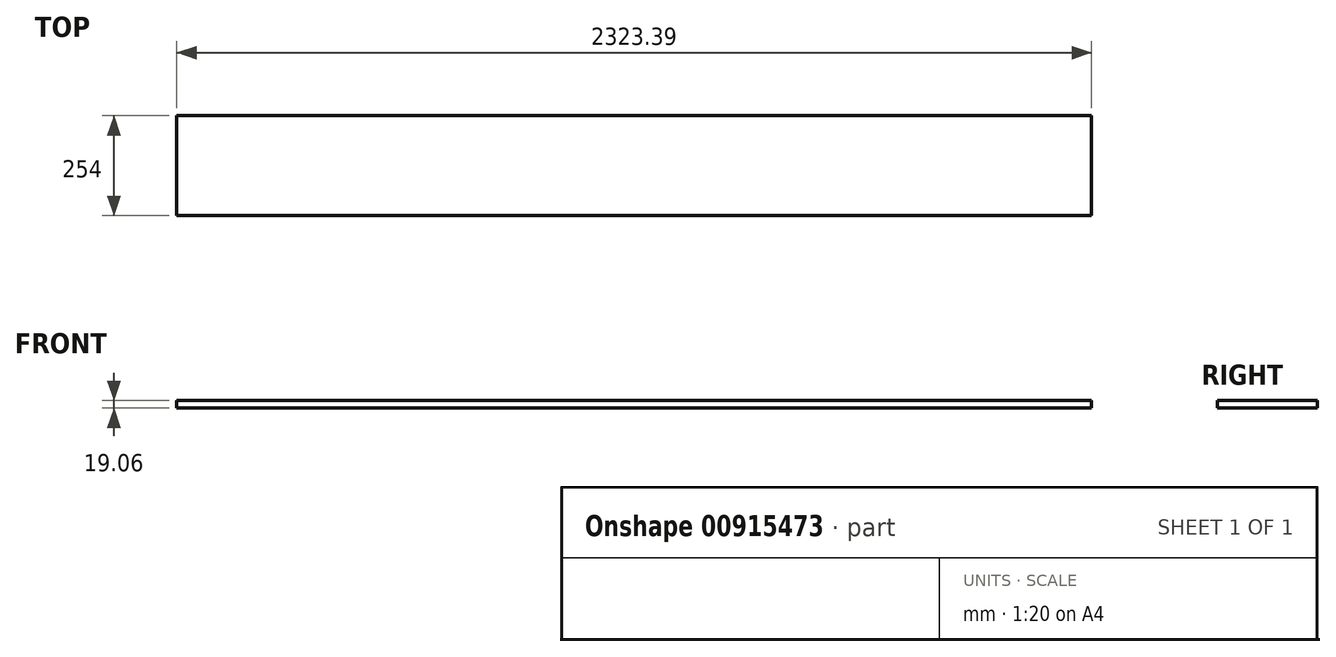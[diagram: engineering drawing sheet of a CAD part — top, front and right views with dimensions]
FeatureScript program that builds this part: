
annotation { "Feature Type Name" : "Feature", "Feature Type Description" : "" }
export const myFeature = defineFeature(function(context is Context, id is Id, definition is map)
    precondition{}
    {
        {
            var Q0;
            Q0=qCreatedBy(makeId("Right.planeOp"),FACE);
            var sketch = newSketch(context, id + "F0", { "sketchPlane" : qUnion([Q0])});
            skLineSegment(sketch, "E0.bottom", {"start": v(127, 9.53) * mm, "end": v(-127, 9.53) * mm});
            skLineSegment(sketch, "E0.top", {"start": v(127, -9.53) * mm, "end": v(-127, -9.53) * mm});
            skLineSegment(sketch, "E0.left", {"start": v(127, 9.53) * mm, "end": v(127, -9.53) * mm});
            skLineSegment(sketch, "E0.right", {"start": v(-127, 9.53) * mm, "end": v(-127, -9.53) * mm});
            skPoint(sketch, "E0.middle", {"position": v(0, 0) * mm});
            skSolve(sketch);
        }
        {
            var Q0;
            Q0=makeQuery(id+"F0.imprint","IMPRINT",FACE,{"disambiguationData":[TD([[makeQuery(id+"F0.imprint","IMPRINT",EDGE,{"derivedFrom":sQuery(id+"F0.wireOp",EDGE,"E0.bottom")}),1.0]])]});
            extrude(context, id + "F1", {"entities" : qUnion([Q0]), "depth" : 2323.39 * mm, "offsetDistance" : 25.4 * mm});
        }
    });
